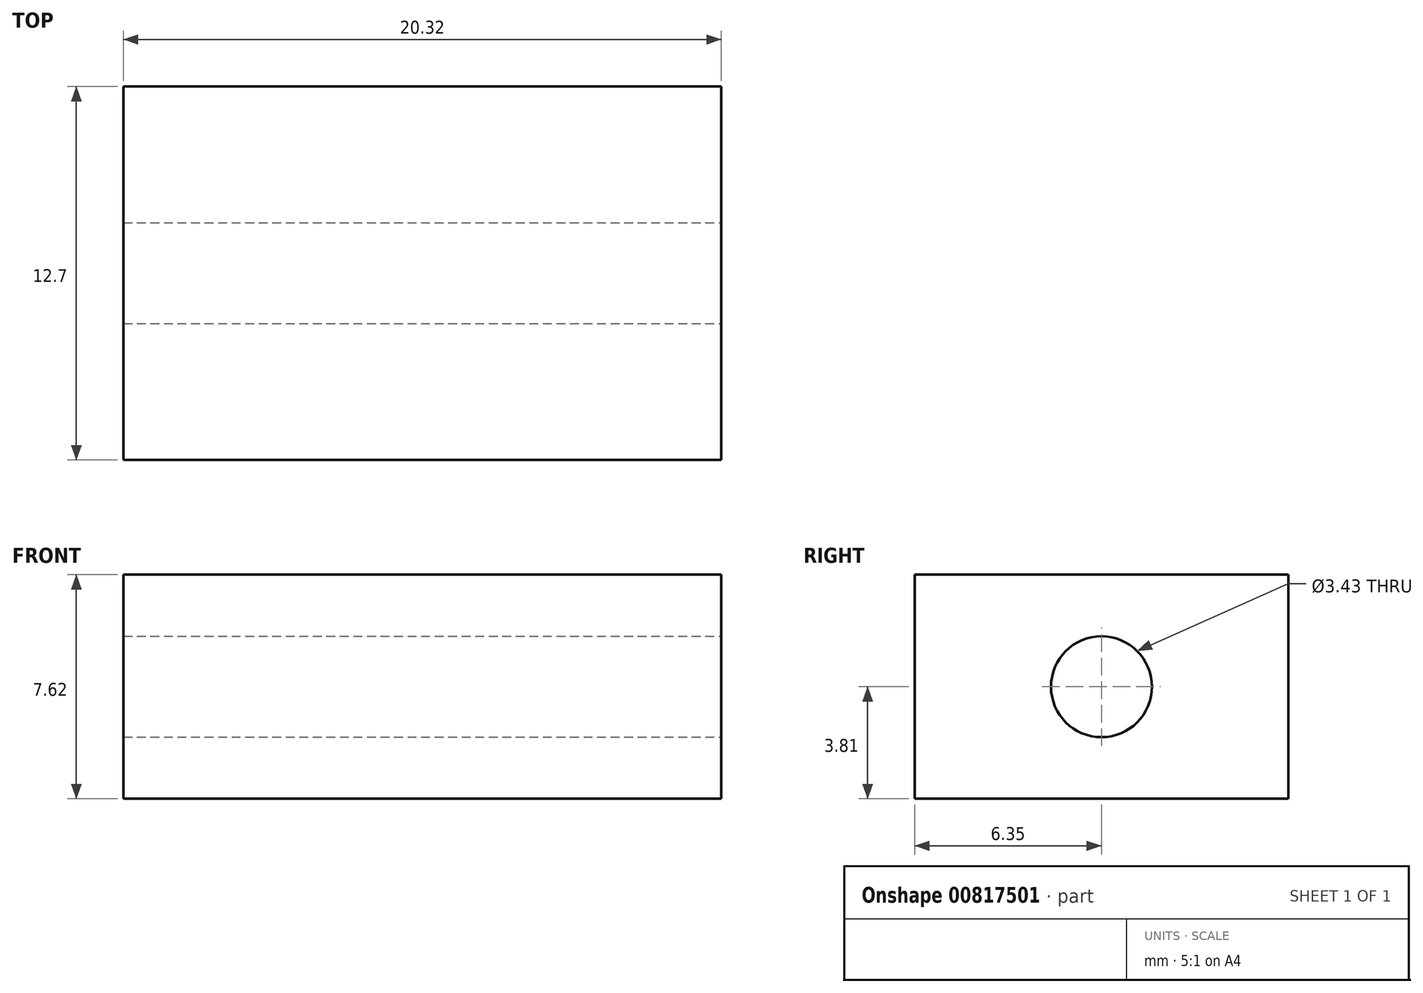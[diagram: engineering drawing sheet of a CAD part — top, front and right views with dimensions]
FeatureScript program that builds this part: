
annotation { "Feature Type Name" : "Feature", "Feature Type Description" : "" }
export const myFeature = defineFeature(function(context is Context, id is Id, definition is map)
    precondition{}
    {
        {
            var Q0;
            Q0=qCreatedBy(makeId("Front.planeOp"),FACE);
            var sketch = newSketch(context, id + "F0", { "sketchPlane" : qUnion([Q0])});
            skLineSegment(sketch, "E0.bottom", {"start": v(10.16, -3.81) * mm, "end": v(-10.16, -3.81) * mm});
            skLineSegment(sketch, "E0.top", {"start": v(10.16, 3.81) * mm, "end": v(-10.16, 3.8) * mm});
            skLineSegment(sketch, "E0.left", {"start": v(10.16, -3.81) * mm, "end": v(10.16, 3.81) * mm});
            skLineSegment(sketch, "E0.right", {"start": v(-10.16, -3.81) * mm, "end": v(-10.16, 3.8) * mm});
            skPoint(sketch, "E0.middle", {"position": v(0, 0) * mm});
            skSolve(sketch);
        }
        {
            var Q0;
            Q0=makeQuery(id+"F0.imprint","IMPRINT",FACE,{"disambiguationData":[TD([[makeQuery(id+"F0.imprint","IMPRINT",EDGE,{"derivedFrom":sQuery(id+"F0.wireOp",EDGE,"E0.bottom")}),-1.0]])]});
            extrude(context, id + "F1", {"entities" : qUnion([Q0]), "depth" : 12.7 * mm, "offsetDistance" : 25.4 * mm});
        }
        {
            var Q0;
            Q0=makeQuery(id+"F1.opExtrude","SWEPT_FACE",FACE,{"disambiguationData":[OSD([sQuery(id+"F0.wireOp",EDGE,"E0.left")])]});
            var sketch = newSketch(context, id + "F2", { "sketchPlane" : qUnion([Q0])});
            skLineSegment(sketch, "E1", {"start": v(0, -3.81) * mm, "end": v(0, 3.81) * mm});
            skCircle(sketch, "E2", {"center": v(-6.35, 0) * mm, "radius": 1.71 * mm});
            skSolve(sketch);
        }
        {
            var Q0;
            Q0=makeQuery(id+"F2.imprint","IMPRINT",FACE,{"disambiguationData":[TD([[makeQuery(id+"F2.imprint","IMPRINT",EDGE,{"derivedFrom":sQuery(id+"F2.wireOp",EDGE,"E2")}),1.0]])]});
            extrude(context, id + "F3", {"entities" : qUnion([Q0]), "operationType" : NewBodyOperationType.REMOVE, "oppositeDirection" : true, "depth" : 20.32 * mm, "offsetDistance" : 25.4 * mm});
        }
    });
